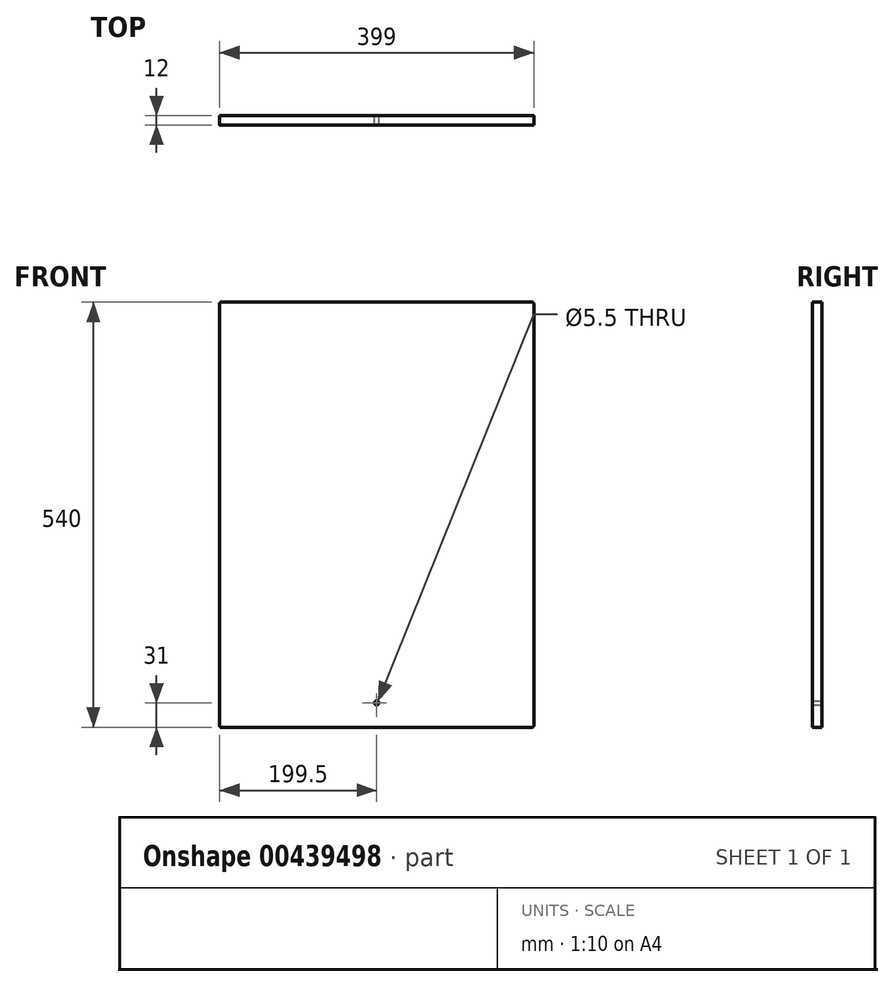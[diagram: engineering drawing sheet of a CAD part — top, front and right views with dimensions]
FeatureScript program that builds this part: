
annotation { "Feature Type Name" : "Feature", "Feature Type Description" : "" }
export const myFeature = defineFeature(function(context is Context, id is Id, definition is map)
    precondition{}
    {
        {
            var Q0;
            Q0=qCreatedBy(makeId("Front.planeOp"),FACE);
            var sketch = newSketch(context, id + "F0", { "sketchPlane" : qUnion([Q0])});
            skLineSegment(sketch, "E0.bottom", {"start": v(-199.5, 540) * mm, "end": v(199.5, 540) * mm});
            skLineSegment(sketch, "E0.top", {"start": v(-199.5, 0) * mm, "end": v(199.5, 0) * mm});
            skLineSegment(sketch, "E0.left", {"start": v(-199.5, 540) * mm, "end": v(-199.5, 0) * mm});
            skLineSegment(sketch, "E0.right", {"start": v(199.5, 540) * mm, "end": v(199.5, 0) * mm});
            skLineSegment(sketch, "E1", {"start": v(0, 540) * mm, "end": v(0, 0) * mm, "construction": true});
            skCircle(sketch, "E2", {"center": v(0, 31) * mm, "radius": 2.75 * mm});
            skSolve(sketch);
        }
        {
            var Q0;
            Q0=makeQuery(id+"F0.imprint","IMPRINT",FACE,{"disambiguationData":[TD([[makeQuery(id+"F0.imprint","IMPRINT",EDGE,{"derivedFrom":sQuery(id+"F0.wireOp",EDGE,"E0.bottom")}),-1.0]])]});
            extrude(context, id + "F1", {"entities" : qUnion([Q0]), "depth" : 12 * mm, "offsetDistance" : 25 * mm});
        }
        {
            var Q0;
            Q0=makeQuery(id+"F1.opExtrude","SWEPT_EDGE",EDGE,{"disambiguationData":[OSD([sQuery(id+"F0.wireOp",EDGE,"E0.bottom"),sQuery(id+"F0.wireOp",EDGE,"E0.left")])]});
            var Q1;
            Q1=makeQuery(id+"F1.opExtrude","SWEPT_EDGE",EDGE,{"disambiguationData":[OSD([sQuery(id+"F0.wireOp",EDGE,"E0.bottom"),sQuery(id+"F0.wireOp",EDGE,"E0.right")])]});
            var Q2;
            Q2=makeQuery(id+"F1.opExtrude","SWEPT_EDGE",EDGE,{"disambiguationData":[OSD([sQuery(id+"F0.wireOp",EDGE,"E0.top"),sQuery(id+"F0.wireOp",EDGE,"E0.right")])]});
            var Q3;
            Q3=makeQuery(id+"F1.opExtrude","SWEPT_EDGE",EDGE,{"disambiguationData":[OSD([sQuery(id+"F0.wireOp",EDGE,"E0.top"),sQuery(id+"F0.wireOp",EDGE,"E0.left")])]});
            fillet(context, id + "F2", {"entities" : qUnion([Q0, Q1, Q2, Q3]), "radius" : 2 * mm, "tangentPropagation" : true, "allowEdgeOverflow" : false});
        }
    });
